# Revit family: AFX-Dean-Outdoor_Flush
name_source: partatom
category: Lighting Fixtures
units: mm (PartAtom-declared; Revit-internal decimal feet)

## family parameters
Cut with Voids When Loaded = No
Host = Face
Light Source = Yes
Part Type = Normal
Room Calculation Point = No
Round Connector Dimension = Use Diameter
Shared = No

## types (2) — shared parameters
Apparent Load = 0 VA
Assembly Code = D5020200
Body Finish = AFX - Black Steel
Color Filter = 16777215
Default Elevation = 48"
Diffuser Finish = AFX - White Acrylic
Dimming Lamp Color Temperature Shift = <None>
Emit Shape Visible in Rendering = No
Emit from Circle Diameter = 5"
Keynote = 12500
Manufacturer = AFX Inc
Photometric Web File = CSM100-12W-30K_IESNA2002.IES
Power Factor = 1
Product Documentation Link = https://www.afxinc.com
Revit File Built By = https://servex-us.com
Tilt Angle = 90.00°
Type Comments = Dean
URL = https://www.afxinc.com
Voltage = 120 V
Wattage Comments = 9

## per-type parameters (varying)
| type | Colour Rendering Index | Description | Diameter | Height |
| DEAW08LAJENBK | 80 | Outdoor LED Ceiling Light Polycarbonate Housing And Diffuser - 8"D x 2"H | 8" | 2" |
| DEAW11LAJENBK | 90 | Outdoor LED Ceiling Light Polycarbonate Housing And Diffuser - 11"D x 2 1/2"H | 11" | 2 51/64" |

note: column(s) folded — value = type name in every type: Model

## geometry (parser evidence)
native form markers: Sweep x2
no freeform markers — native parametric forms only
